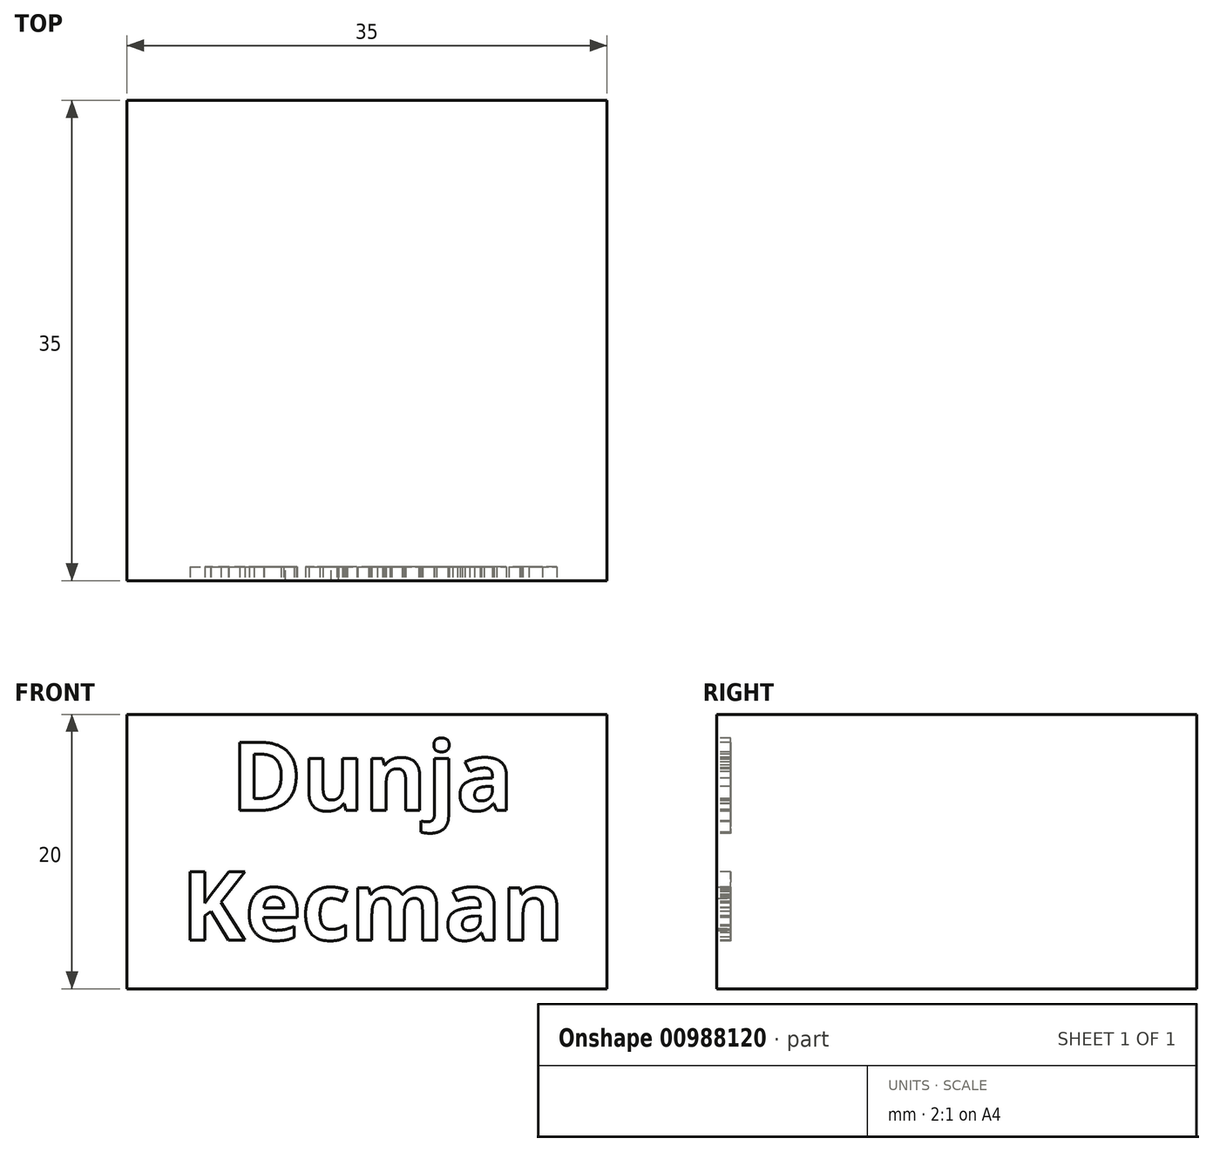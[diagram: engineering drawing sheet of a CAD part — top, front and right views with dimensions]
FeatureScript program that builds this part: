
annotation { "Feature Type Name" : "Feature", "Feature Type Description" : "" }
export const myFeature = defineFeature(function(context is Context, id is Id, definition is map)
    precondition{}
    {
        {
            var Q0;
            Q0=qCreatedBy(makeId("Top.planeOp"),FACE);
            var sketch = newSketch(context, id + "F0", { "sketchPlane" : qUnion([Q0])});
            skLineSegment(sketch, "E0.bottom", {"start": v(0, 0) * mm, "end": v(35, 0) * mm});
            skLineSegment(sketch, "E0.top", {"start": v(0, 35) * mm, "end": v(35, 35) * mm});
            skLineSegment(sketch, "E0.left", {"start": v(0, 0) * mm, "end": v(0, 35) * mm});
            skLineSegment(sketch, "E0.right", {"start": v(35, 0) * mm, "end": v(35, 35) * mm});
            skSolve(sketch);
        }
        {
            var Q0;
            Q0 = qSketchRegion(id + "F0", true);
            extrude(context, id + "F1", {"entities" : qUnion([Q0]), "depth" : 20 * mm, "offsetDistance" : 25 * mm});
        }
        {
            var Q0;
            Q0=makeQuery(id+"F1.opExtrude","SWEPT_FACE",FACE,{"disambiguationData":[OSD([sQuery(id+"F0.wireOp",EDGE,"E0.bottom")])]});
            var sketch = newSketch(context, id + "F2", { "sketchPlane" : qUnion([Q0])});
            skText(sketch, "E1", { "text": "  Dunja\nKecman", "fontName": "OpenSans-Bold.ttf"});
            const initialGuessF2  = {"E1": [0.004, 0.013, 1, 0, 0.005]};
            skSetInitialGuess(sketch, initialGuessF2);
            skSolve(sketch);
        }
        {
            var Q0;
            Q0 = qSketchRegion(id + "F2", true);
            extrude(context, id + "F3", {"entities" : qUnion([Q0]), "operationType" : NewBodyOperationType.REMOVE, "oppositeDirection" : true, "depth" : 1 * mm, "offsetDistance" : 25 * mm});
        }
    });
